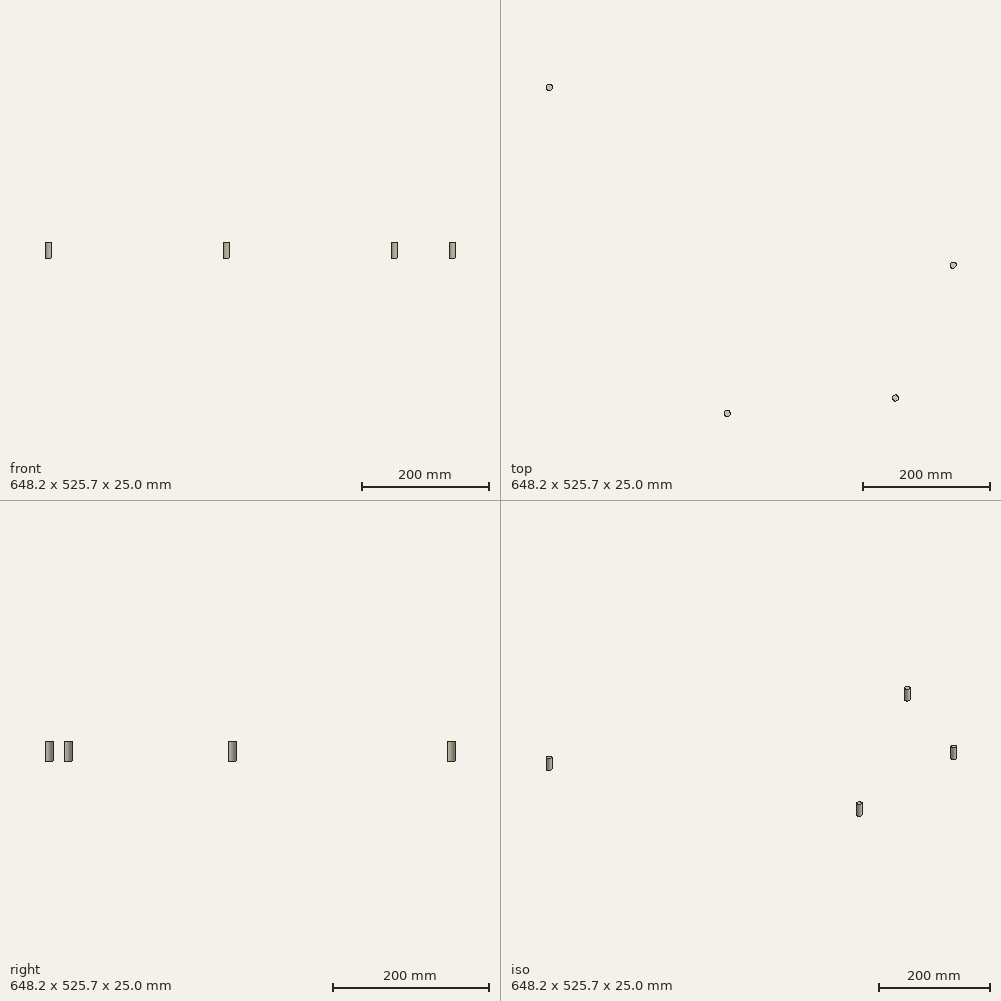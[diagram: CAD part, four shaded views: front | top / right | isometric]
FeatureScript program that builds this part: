
annotation { "Feature Type Name" : "Feature", "Feature Type Description" : "" }
export const myFeature = defineFeature(function(context is Context, id is Id, definition is map)
    precondition{}
    {
        {
            var Q0;
            Q0=qCreatedBy(makeId("Top.planeOp"),FACE);
            var sketch = newSketch(context, id + "F0", { "sketchPlane" : qUnion([Q0])});
            skCircle(sketch, "E0", {"center": v(-374.15, 281.24) * mm, "radius": 5 * mm});
            skCircle(sketch, "E1", {"center": v(-93.43, -234.47) * mm, "radius": 5 * mm});
            skCircle(sketch, "E2", {"center": v(172.8, -210.02) * mm, "radius": 5 * mm});
            skCircle(sketch, "E3", {"center": v(264.05, 0) * mm, "radius": 5 * mm});
            skSolve(sketch);
        }
        {
            var Q0;
            Q0 = qSketchRegion(id + "F0", true);
            extrude(context, id + "F1", {"entities" : qUnion([Q0]), "depth" : 25 * mm});
        }
    });
